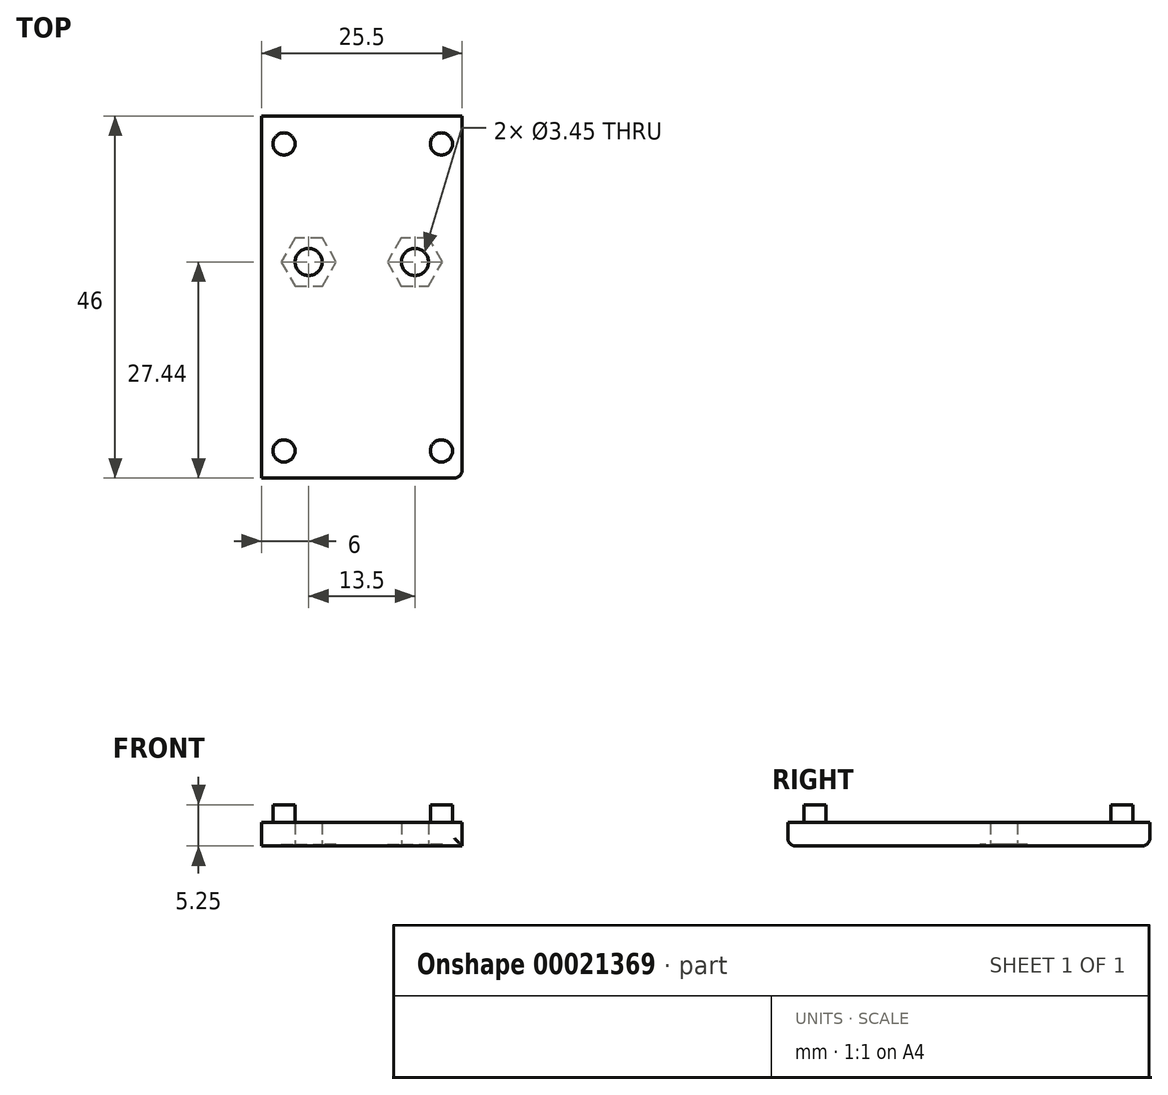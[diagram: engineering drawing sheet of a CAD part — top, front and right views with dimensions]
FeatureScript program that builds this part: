
annotation { "Feature Type Name" : "Feature", "Feature Type Description" : "" }
export const myFeature = defineFeature(function(context is Context, id is Id, definition is map)
    precondition{}
    {
        {
            var Q0;
            Q0=qCreatedBy(makeId("Top.planeOp"),FACE);
            var sketch = newSketch(context, id + "F0", { "sketchPlane" : qUnion([Q0])});
            skLineSegment(sketch, "E0.rect.bottom", {"start": v(12.75, -23) * mm, "end": v(-12.75, -23) * mm});
            skLineSegment(sketch, "E0.rect.top", {"start": v(12.75, 23) * mm, "end": v(-12.75, 23) * mm});
            skLineSegment(sketch, "E0.rect.left", {"start": v(12.75, -23) * mm, "end": v(12.75, 23) * mm});
            skLineSegment(sketch, "E0.rect.right", {"start": v(-12.75, -23) * mm, "end": v(-12.75, 23) * mm});
            skPoint(sketch, "E0.rect.middle", {"position": v(0, 0) * mm});
            skSolve(sketch);
        }
        {
            var Q0;
            Q0 = qSketchRegion(id + "F0", true);
            extrude(context, id + "F1", {"entities" : qUnion([Q0]), "depth" : 3 * mm});
        }
        {
            var Q0;
            Q0=makeQuery(id+"F1.opExtrude","CAP_FACE",FACE,{"disambiguationData":[OSD([sQuery(id+"F0.wireOp",EDGE,"E0.rect.bottom"),sQuery(id+"F0.wireOp",EDGE,"E0.rect.top"),sQuery(id+"F0.wireOp",EDGE,"E0.rect.left"),sQuery(id+"F0.wireOp",EDGE,"E0.rect.right")])],"isStart":false});
            var sketch = newSketch(context, id + "F2", { "sketchPlane" : qUnion([Q0])});
            skCircle(sketch, "E1", {"center": v(10.12, -19.56) * mm, "radius": 1.41 * mm});
            skCircle(sketch, "E2", {"center": v(10.12, 19.44) * mm, "radius": 1.41 * mm});
            skCircle(sketch, "E3", {"center": v(-9.88, -19.56) * mm, "radius": 1.41 * mm});
            skCircle(sketch, "E4", {"center": v(-9.88, 19.44) * mm, "radius": 1.41 * mm});
            skSolve(sketch);
        }
        {
            var Q0;
            Q0 = qSketchRegion(id + "F2", true);
            extrude(context, id + "F3", {"entities" : qUnion([Q0]), "operationType" : NewBodyOperationType.ADD, "depth" : 2.25 * mm});
        }
        {
            var Q0;
            Q0=makeQuery(id+"F1.opExtrude","CAP_FACE",FACE,{"disambiguationData":[OSD([sQuery(id+"F0.wireOp",EDGE,"E0.rect.bottom"),sQuery(id+"F0.wireOp",EDGE,"E0.rect.top"),sQuery(id+"F0.wireOp",EDGE,"E0.rect.left"),sQuery(id+"F0.wireOp",EDGE,"E0.rect.right")])],"isStart":true});
            var sketch = newSketch(context, id + "F4", { "sketchPlane" : qUnion([Q0])});
            skCircle(sketch, "E5.cCircle", {"center": v(-6.75, -4.44) * mm, "radius": 3.03 * mm, "construction": true});
            skLineSegment(sketch, "E5.0", {"start": v(-8.5, -1.4) * mm, "end": v(-5, -1.4) * mm});
            skLineSegment(sketch, "E5.1", {"start": v(-5, -1.4) * mm, "end": v(-3.25, -4.44) * mm});
            skLineSegment(sketch, "E5.2", {"start": v(-3.25, -4.44) * mm, "end": v(-5, -7.47) * mm});
            skLineSegment(sketch, "E5.3", {"start": v(-5, -7.47) * mm, "end": v(-8.5, -7.47) * mm});
            skLineSegment(sketch, "E5.4", {"start": v(-8.5, -7.47) * mm, "end": v(-10.25, -4.44) * mm});
            skLineSegment(sketch, "E5.5", {"start": v(-10.25, -4.44) * mm, "end": v(-8.5, -1.4) * mm});
            skPoint(sketch, "E5.0.midPoint", {"position": v(-6.75, -1.4) * mm});
            skCircle(sketch, "E6.cCircle", {"center": v(6.75, -4.44) * mm, "radius": 3.03 * mm, "construction": true});
            skLineSegment(sketch, "E6.0", {"start": v(5, -1.4) * mm, "end": v(8.5, -1.4) * mm});
            skLineSegment(sketch, "E6.1", {"start": v(8.5, -1.4) * mm, "end": v(10.25, -4.44) * mm});
            skLineSegment(sketch, "E6.2", {"start": v(10.25, -4.44) * mm, "end": v(8.5, -7.47) * mm});
            skLineSegment(sketch, "E6.3", {"start": v(8.5, -7.47) * mm, "end": v(5, -7.47) * mm});
            skLineSegment(sketch, "E6.4", {"start": v(5, -7.47) * mm, "end": v(3.25, -4.44) * mm});
            skLineSegment(sketch, "E6.5", {"start": v(3.25, -4.44) * mm, "end": v(5, -1.4) * mm});
            skPoint(sketch, "E6.0.midPoint", {"position": v(6.75, -1.4) * mm});
            skSolve(sketch);
        }
        {
            var Q0;
            Q0 = qSketchRegion(id + "F4", true);
            extrude(context, id + "F5", {"entities" : qUnion([Q0]), "operationType" : NewBodyOperationType.REMOVE, "oppositeDirection" : true, "depth" : 0.2 * mm});
        }
        {
            var Q0;
            Q0=makeQuery(id+"F5.boolean.opBoolean","COPY",FACE,{"derivedFrom":makeQuery(id+"F5.opExtrude","CAP_FACE",FACE,{"disambiguationData":[OSD([sQuery(id+"F4.wireOp",EDGE,"E5.0"),sQuery(id+"F4.wireOp",EDGE,"E5.1"),sQuery(id+"F4.wireOp",EDGE,"E5.2"),sQuery(id+"F4.wireOp",EDGE,"E5.3"),sQuery(id+"F4.wireOp",EDGE,"E5.4"),sQuery(id+"F4.wireOp",EDGE,"E5.5")])],"isStart":false})});
            var sketch = newSketch(context, id + "F6", { "sketchPlane" : qUnion([Q0])});
            skLineSegment(sketch, "E7", {"start": v(-10.25, -4.44) * mm, "end": v(-3.25, -4.44) * mm, "construction": true});
            skLineSegment(sketch, "E8", {"start": v(-6.75, -7.47) * mm, "end": v(-6.75, -1.4) * mm, "construction": true});
            skCircle(sketch, "E9", {"center": v(-6.75, -4.44) * mm, "radius": 1.73 * mm});
            skCircle(sketch, "E10", {"center": v(6.75, -4.44) * mm, "radius": 1.73 * mm});
            skSolve(sketch);
        }
        {
            var Q0;
            Q0 = qSketchRegion(id + "F6", true);
            extrude(context, id + "F7", {"entities" : qUnion([Q0]), "operationType" : NewBodyOperationType.REMOVE, "endBound" : BoundingType.THROUGH_ALL, "oppositeDirection" : true, "depth" : 25 * mm});
        }
        {
            var Q0;
            Q0=makeQuery(id+"F1.opExtrude","SWEPT_EDGE",EDGE,{"disambiguationData":[OSD([sQuery(id+"F0.wireOp",EDGE,"E0.rect.bottom"),sQuery(id+"F0.wireOp",EDGE,"E0.rect.left")])]});
            fillet(context, id + "F8", {"entities" : qUnion([Q0]), "radius" : 1 * mm, "tangentPropagation" : true, "allowEdgeOverflow" : false});
        }
        {
            var Q0;
            Q0=makeQuery(id+"F1.opExtrude","CAP_EDGE",EDGE,{"disambiguationData":[OSD([sQuery(id+"F0.wireOp",EDGE,"E0.rect.top")])],"isStart":true});
            var Q1;
            Q1=makeQuery(id+"F1.opExtrude","CAP_EDGE",EDGE,{"disambiguationData":[OSD([sQuery(id+"F0.wireOp",EDGE,"E0.rect.bottom")])],"isStart":true});
            fillet(context, id + "F9", {"entities" : qUnion([Q0, Q1]), "radius" : 1 * mm, "allowEdgeOverflow" : false});
        }
    });
